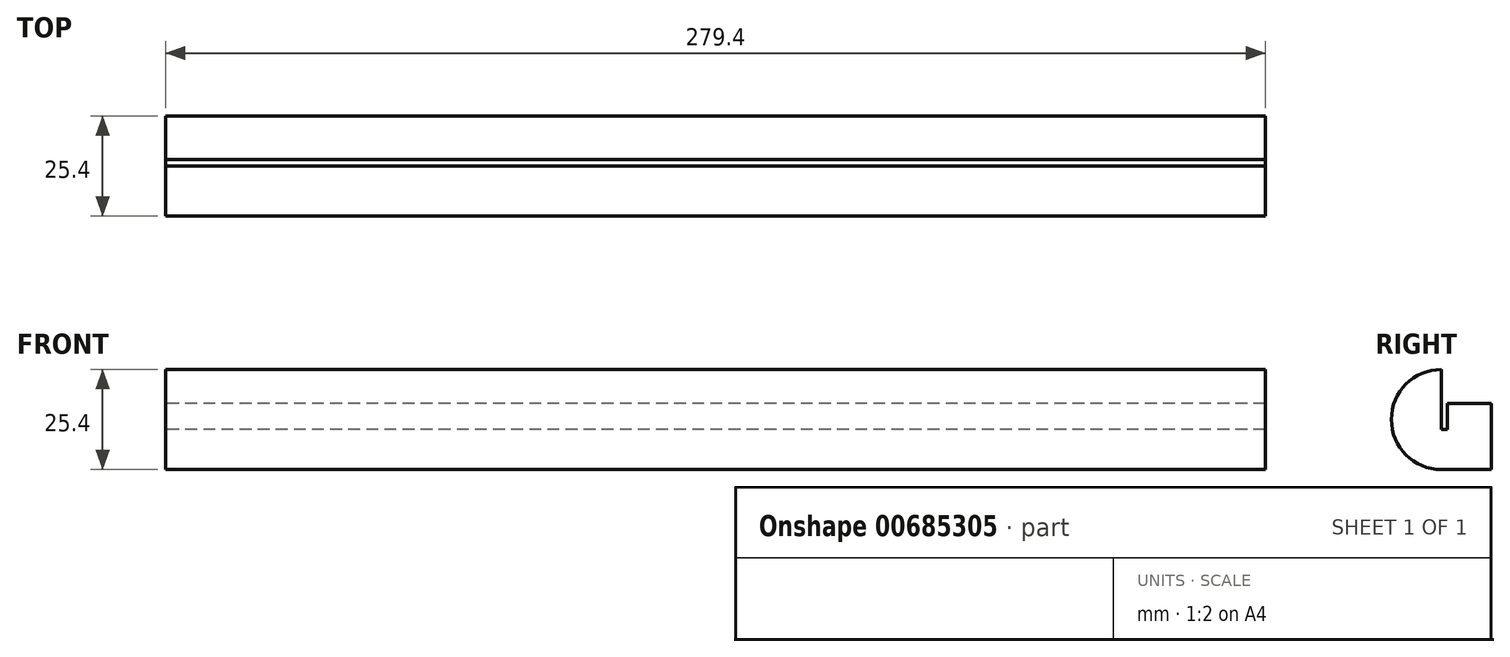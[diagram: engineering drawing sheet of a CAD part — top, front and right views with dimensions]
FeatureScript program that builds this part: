
annotation { "Feature Type Name" : "Feature", "Feature Type Description" : "" }
export const myFeature = defineFeature(function(context is Context, id is Id, definition is map)
    precondition{}
    {
        {
            var Q0;
            Q0=qCreatedBy(makeId("Right.planeOp"),FACE);
            var sketch = newSketch(context, id + "F0", { "sketchPlane" : qUnion([Q0])});
            skLineSegment(sketch, "E0", {"start": v(0, 0) * mm, "end": v(0, -25.4) * mm});
            skLineSegment(sketch, "E1", {"start": v(0, -25.4) * mm, "end": v(12.7, -25.4) * mm});
            skArc(sketch, "E2", {"start": v(0, 0) * mm, "mid": v(-12.7, -12.7) * mm, "end": v(0, -25.4) * mm});
            skLineSegment(sketch, "E3", {"start": v(12.7, -25.4) * mm, "end": v(12.7, -8.67) * mm});
            skLineSegment(sketch, "E4", {"start": v(12.7, -8.67) * mm, "end": v(1.6, -8.67) * mm});
            skLineSegment(sketch, "E5", {"start": v(1.6, -8.67) * mm, "end": v(1.6, -15.2) * mm});
            skLineSegment(sketch, "E6", {"start": v(1.6, -15.2) * mm, "end": v(0, -15.2) * mm});
            skSolve(sketch);
        }
        {
            var Q0;
            Q0 = qSketchRegion(id + "F0", true);
            extrude(context, id + "F1", {"entities" : qUnion([Q0]), "depth" : 279.4 * mm, "offsetDistance" : 25.4 * mm});
        }
    });
